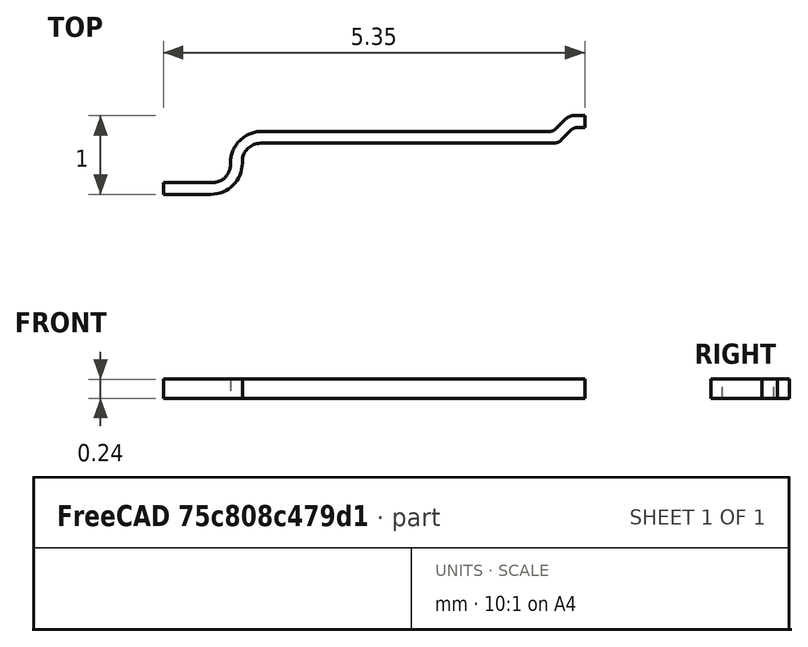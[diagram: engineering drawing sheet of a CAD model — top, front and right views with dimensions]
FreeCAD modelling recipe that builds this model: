
FCSTD DOCUMENT  (FreeCAD 0.17R12607 (Git))
Label: U02-BFD3111B0-009 Pin
License: CreativeCommons Attribution-ShareAlike
LicenseURL: http://creativecommons.org/licenses/by-sa/4.0/
objects: Sketcher::SketchObject×1, PartDesign::Pad×1, PartDesign::Body×1
note: 4 computed .brp shape members not serialized (recipe doc carries the construction recipe); baked Part::Feature solids carry a one-line shape summary decoded from their .brp

FEATURE [Sketcher::SketchObject] Sketch
  MapMode = 5
  Support = -> [XY_Plane]
  sketch-geometry (23):
    g0: LineSegment [constr] StartX=0 StartY=0 StartZ=0 EndX=5.35 EndY=0 EndZ=0
    g1: LineSegment [constr] StartX=5.35 StartY=0 StartZ=0 EndX=5.35 EndY=1 EndZ=0
    g2: LineSegment [constr] StartX=5.35 StartY=1 StartZ=0 EndX=0 EndY=1 EndZ=0
    g3: LineSegment [constr] StartX=0 StartY=1 StartZ=0 EndX=0 EndY=0 EndZ=0
    g4: LineSegment StartX=0 StartY=0 StartZ=0 EndX=0.6 EndY=0 EndZ=0
    g5: LineSegment StartX=0.619181 StartY=0.15 StartZ=0 EndX=0 EndY=0.15 EndZ=0
    g6: LineSegment StartX=0 StartY=0.15 StartZ=0 EndX=0 EndY=0 EndZ=0
    g7: LineSegment StartX=1.24982 StartY=0.8 StartZ=0 EndX=4.90858 EndY=0.8 EndZ=0
    g8: LineSegment StartX=5.35 StartY=1 StartZ=0 EndX=5.21213 EndY=1 EndZ=0
    g9: LineSegment StartX=5.25355 StartY=0.85 StartZ=0 EndX=5.35 EndY=0.85 EndZ=0
    g10: LineSegment StartX=5.35 StartY=0.85 StartZ=0 EndX=5.35 EndY=1 EndZ=0
    g11: LineSegment StartX=4.97929 StartY=0.829289 StartZ=0 EndX=5.10607 EndY=0.956066 EndZ=0
    g12: LineSegment StartX=5.05607 StartY=0.693934 StartZ=0 EndX=5.18284 EndY=0.820711 EndZ=0
    g13: LineSegment StartX=4.95 StartY=0.65 StartZ=0 EndX=1.23092 EndY=0.65 EndZ=0
    g14: LineSegment StartX=1 StartY=0.419076 StartZ=0 EndX=1 EndY=0.4 EndZ=0
    g15: ArcOfCircle CenterX=0.6 CenterY=0.4 CenterZ=0 NormalX=0 NormalY=0 NormalZ=1 AngleXU=0 Radius=0.4 StartAngle=4.71239 EndAngle=6.28319
    g16: ArcOfCircle CenterX=1.23092 CenterY=0.419076 CenterZ=0 NormalX=0 NormalY=0 NormalZ=1 AngleXU=0 Radius=0.230924 StartAngle=1.5708 EndAngle=3.14159
    g17: ArcOfCircle CenterX=4.90858 CenterY=0.9 CenterZ=0 NormalX=0 NormalY=0 NormalZ=1 AngleXU=0 Radius=0.1 StartAngle=4.71239 EndAngle=5.49779
    g18: ArcOfCircle CenterX=4.95 CenterY=0.8 CenterZ=0 NormalX=0 NormalY=0 NormalZ=1 AngleXU=0 Radius=0.15 StartAngle=4.71239 EndAngle=5.49779
    g19: ArcOfCircle CenterX=5.25355 CenterY=0.75 CenterZ=0 NormalX=0 NormalY=0 NormalZ=1 AngleXU=0 Radius=0.1 StartAngle=1.5708 EndAngle=2.35619
    g20: ArcOfCircle CenterX=5.21213 CenterY=0.85 CenterZ=0 NormalX=0 NormalY=0 NormalZ=1 AngleXU=0 Radius=0.15 StartAngle=1.5708 EndAngle=2.35619
    g21: ArcOfCircle CenterX=1.24982 CenterY=0.4 CenterZ=0 NormalX=0 NormalY=0 NormalZ=1 AngleXU=0 Radius=0.4 StartAngle=1.5708 EndAngle=3.17183
    g22: ArcOfCircle CenterX=0.619182 CenterY=0.380924 CenterZ=0 NormalX=0 NormalY=0 NormalZ=1 AngleXU=0 Radius=0.230924 StartAngle=4.71239 EndAngle=6.31342
  constraints (62):
    c: Coincident(g0,g1)
    c: Coincident(g1,g2)
    c: Coincident(g2,g3)
    c: Coincident(g3,g0)
    c: Horizontal(g0)
    c: Horizontal(g2)
    c: Vertical(g1)
    c: Vertical(g3)
    c: Coincident(g0,g-1)
    c: DistanceY(g1,g1) = 1
    c: DistanceX(g2,g2) = 5.35
    c: Coincident(g5,g6)
    c: Coincident(g6,g4)
    c: Horizontal(g4)
    c: Horizontal(g5)
    c: Vertical(g6)
    c: Coincident(g4,g-1)
    c: Horizontal(g7)
    c: Coincident(g9,g10)
    c: Coincident(g10,g8)
    c: Horizontal(g8)
    c: Horizontal(g9)
    c: Vertical(g10)
    c: PointOnObject(g8,g1)
    c: Horizontal(g13)
    c: Vertical(g14)
    c: DistanceY(g6,g6) = 0.15
    c: Equal(g6,g10)
    c: Parallel(g12,g11)
    c: PointOnObject(g8,g2)
    c: Angle(g12,g13) = 2.35619
    c: Distance(g-1,g14) = 1
    c: Distance(g-1,g7) = 0.8
    c: Tangent(g14,g15) = 1.5708
    c: Tangent(g4,g15) = -1.5708
    c: Tangent(g14,g16) = -1.5708
    c: Tangent(g13,g16) = -1.5708
    c: Tangent(g7,g17) = -1.5708
    c: Tangent(g11,g17) = -1.5708
    c: Tangent(g13,g18) = 1.5708
    c: Tangent(g12,g18) = -1.5708
    c: Tangent(g9,g19) = 1.5708
    c: Tangent(g12,g19) = 1.5708
    c: Tangent(g8,g20) = -1.5708
    c: Tangent(g11,g20) = 1.5708
    c: Radius(g15) = 0.4
    c: Coincident(g21,g7)
    c: Coincident(g22,g5)
    c: Coincident(g22,g21)
    c: Tangent(g7,g21)
    c: Tangent(g21,g22)
    c: Tangent(g22,g5)
    c: Equal(g15,g21)
    c: Equal(g22,g16)
    c: Distance(g13,g7) = 0.15
    c: Distance(g21,g14) = 0.15
    c: Radius(g18) = 0.15
    c: Radius(g17) = 0.1
    c: Equal(g18,g20)
    c: Equal(g19,g17)
    c: Distance(g11,g12) = 0.15
    c: Distance(g13,g10) = 0.4
FEATURE [PartDesign::Pad] Pad
  Length = 0.25
  Length2 = 100
  Midplane = true
  Profile = -> Sketch
  Type = 0
FEATURE [PartDesign::Body] Body
  Group = -> [Sketch,Pad]
  Origin = -> Origin
  Tip = -> Pad
